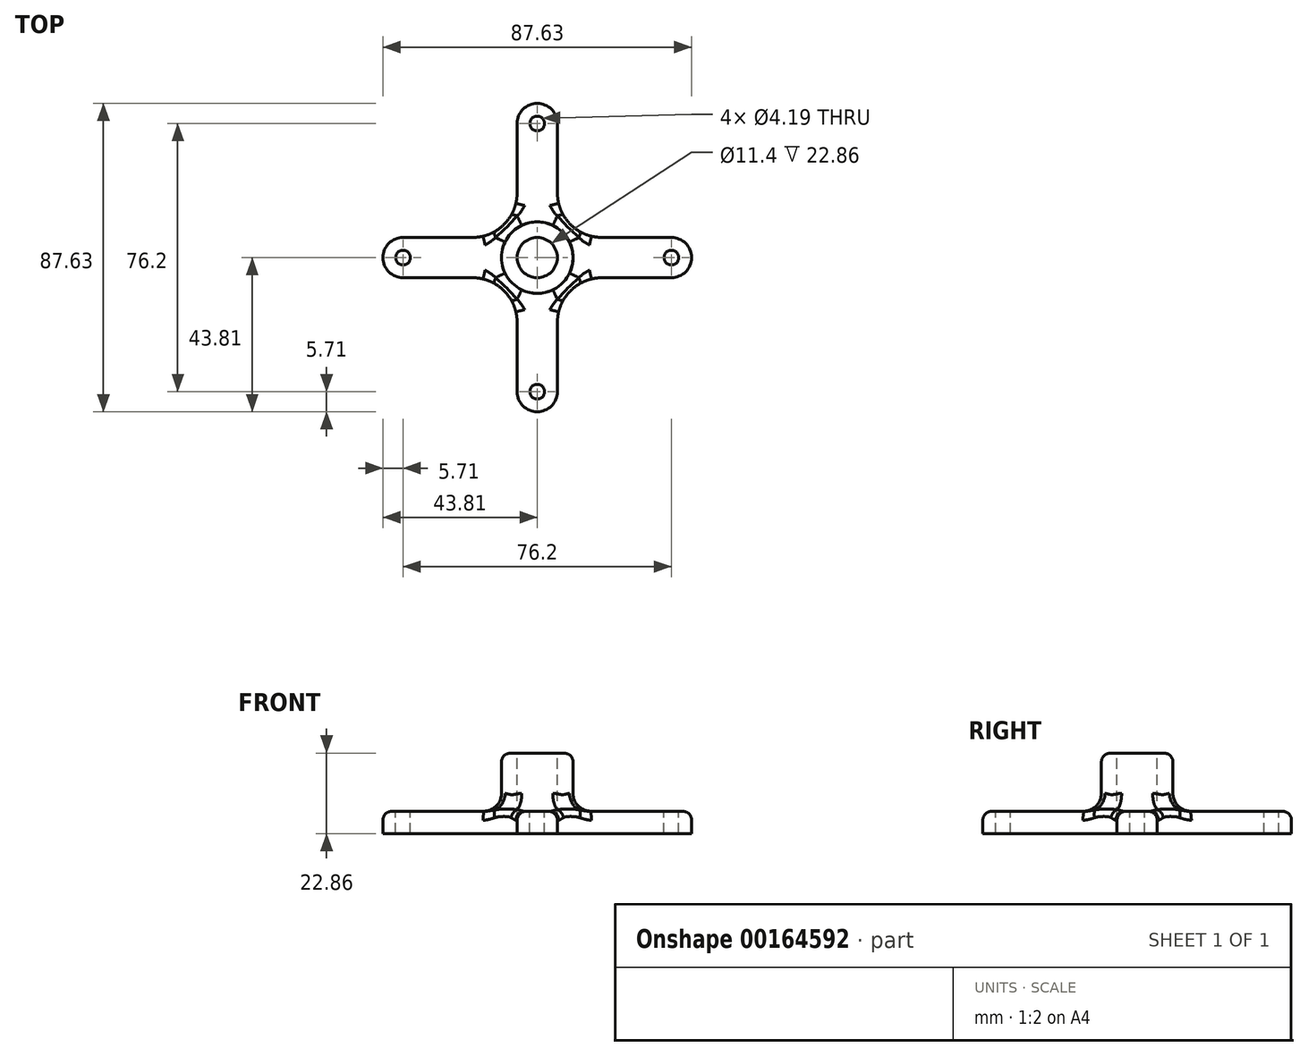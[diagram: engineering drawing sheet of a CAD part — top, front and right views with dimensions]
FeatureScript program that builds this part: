
annotation { "Feature Type Name" : "Feature", "Feature Type Description" : "" }
export const myFeature = defineFeature(function(context is Context, id is Id, definition is map)
    precondition{}
    {
        {
            var Q0;
            Q0=qCreatedBy(makeId("Top.planeOp"),FACE);
            var sketch = newSketch(context, id + "F0", { "sketchPlane" : qUnion([Q0])});
            skArc(sketch, "E0", {"start": v(5.71, 38.1) * mm, "mid": v(0, 43.81) * mm, "end": v(-5.72, 38.1) * mm});
            skArc(sketch, "E1", {"start": v(38.1, -5.71) * mm, "mid": v(43.81, 0) * mm, "end": v(38.1, 5.72) * mm});
            skArc(sketch, "E2", {"start": v(-5.72, -38.1) * mm, "mid": v(0, -43.81) * mm, "end": v(5.72, -38.1) * mm});
            skArc(sketch, "E3", {"start": v(-38.1, 5.72) * mm, "mid": v(-43.81, 0) * mm, "end": v(-38.1, -5.72) * mm});
            skLineSegment(sketch, "E4.top", {"start": v(-5.72, 1.59) * mm, "end": v(-4.64, 1.59) * mm});
            skLineSegment(sketch, "E4.left", {"start": v(-5.72, 38.1) * mm, "end": v(-5.72, 18.42) * mm});
            skLineSegment(sketch, "E4.right", {"start": v(5.71, 38.1) * mm, "end": v(5.71, 18.42) * mm});
            skPoint(sketch, "E4.middle", {"position": v(0, 19.84) * mm});
            skLineSegment(sketch, "E5.bottom", {"start": v(-38.1, -5.72) * mm, "end": v(-18.41, -5.72) * mm});
            skLineSegment(sketch, "E5.top", {"start": v(-38.1, 5.72) * mm, "end": v(-18.41, 5.72) * mm});
            skPoint(sketch, "E5.middle", {"position": v(-20.1, 0) * mm});
            skLineSegment(sketch, "E6.bottom", {"start": v(38.1, 5.72) * mm, "end": v(18.41, 5.72) * mm});
            skLineSegment(sketch, "E6.top", {"start": v(38.1, -5.72) * mm, "end": v(18.41, -5.72) * mm});
            skPoint(sketch, "E6.middle", {"position": v(16.73, 0) * mm});
            skLineSegment(sketch, "E7.top", {"start": v(-5.72, -2.38) * mm, "end": v(-4.64, -2.38) * mm});
            skLineSegment(sketch, "E7.left", {"start": v(-5.72, -38.1) * mm, "end": v(-5.72, -18.41) * mm});
            skLineSegment(sketch, "E7.right", {"start": v(5.72, -38.1) * mm, "end": v(5.72, -18.42) * mm});
            skPoint(sketch, "E7.middle", {"position": v(0, -20.24) * mm});
            skPoint(sketch, "E8.newPointA", {"position": v(-2.12, 5.72) * mm});
            skArc(sketch, "E8.filletArc", {"start": v(-18.41, 5.72) * mm, "mid": v(-9.43, 9.43) * mm, "end": v(-5.71, 18.42) * mm});
            skPoint(sketch, "E9.newPointB", {"position": v(-4.64, 5.72) * mm});
            skArc(sketch, "E9.filletArc", {"start": v(5.71, 18.42) * mm, "mid": v(9.43, 9.43) * mm, "end": v(18.41, 5.72) * mm});
            skPoint(sketch, "E10.newPointA", {"position": v(-4.64, -5.72) * mm});
            skArc(sketch, "E10.filletArc", {"start": v(18.41, -5.72) * mm, "mid": v(9.43, -9.43) * mm, "end": v(5.71, -18.42) * mm});
            skPoint(sketch, "E11.newPointB", {"position": v(-2.12, -5.72) * mm});
            skArc(sketch, "E11.filletArc", {"start": v(-5.71, -18.41) * mm, "mid": v(-9.43, -9.43) * mm, "end": v(-18.41, -5.71) * mm});
            skPoint(sketch, "E12.center.orphan", {"position": v(0, 0) * mm});
            skPoint(sketch, "E13.orphan", {"position": v(5.71, 1.59) * mm});
            skPoint(sketch, "E14.trimOffspring.end.orphan", {"position": v(5.72, -2.38) * mm});
            skCircle(sketch, "E15", {"center": v(0, 0) * mm, "radius": 10.16 * mm});
            skSolve(sketch);
        }
        {
            var Q0;
            Q0 = qSketchRegion(id + "F0", true);
            var Q1;
            Q1=makeQuery(id+"F0.imprint","IMPRINT",FACE,{"disambiguationData":[TD([[makeQuery(id+"F0.imprint","IMPRINT",EDGE,{"derivedFrom":sQuery(id+"F0.wireOp",EDGE,"E15")}),1.0]])]});
            extrude(context, id + "F1", {"entities" : qUnion([Q0, Q1]), "depth" : 6.35 * mm});
        }
        {
            var Q0;
            Q0=makeQuery(id+"F0.imprint","IMPRINT",FACE,{"disambiguationData":[TD([[makeQuery(id+"F0.imprint","IMPRINT",EDGE,{"derivedFrom":sQuery(id+"F0.wireOp",EDGE,"E15")}),1.0]])]});
            extrude(context, id + "F2", {"entities" : qUnion([Q0]), "operationType" : NewBodyOperationType.ADD, "depth" : 22.86 * mm});
        }
        {
            var Q0;
            Q0=makeQuery(id+"F2.opExtrude","CAP_FACE",FACE,{"disambiguationData":[OSD([sQuery(id+"F0.wireOp",EDGE,"E15")])],"isStart":false});
            var sketch = newSketch(context, id + "F3", { "sketchPlane" : qUnion([Q0])});
            skCircle(sketch, "E16", {"center": v(0, 0) * mm, "radius": 5.7 * mm});
            skSolve(sketch);
        }
        {
            var Q0;
            Q0 = qSketchRegion(id + "F3", true);
            extrude(context, id + "F4", {"entities" : qUnion([Q0]), "operationType" : NewBodyOperationType.REMOVE, "endBound" : BoundingType.THROUGH_ALL, "oppositeDirection" : true, "depth" : 25.4 * mm});
        }
        {
            var Q0;
            Q0=makeQuery(id+"F1.opExtrude","CAP_FACE",FACE,{"disambiguationData":[OSD([sQuery(id+"F0.wireOp",EDGE,"E0"),sQuery(id+"F0.wireOp",EDGE,"E1"),sQuery(id+"F0.wireOp",EDGE,"E2"),sQuery(id+"F0.wireOp",EDGE,"E3"),sQuery(id+"F0.wireOp",EDGE,"E4.left"),sQuery(id+"F0.wireOp",EDGE,"E4.right"),sQuery(id+"F0.wireOp",EDGE,"E5.bottom"),sQuery(id+"F0.wireOp",EDGE,"E5.top"),sQuery(id+"F0.wireOp",EDGE,"E6.bottom"),sQuery(id+"F0.wireOp",EDGE,"E6.top"),sQuery(id+"F0.wireOp",EDGE,"E7.left"),sQuery(id+"F0.wireOp",EDGE,"E7.right"),sQuery(id+"F0.wireOp",EDGE,"E8.filletArc"),sQuery(id+"F0.wireOp",EDGE,"E9.filletArc"),sQuery(id+"F0.wireOp",EDGE,"E10.filletArc"),sQuery(id+"F0.wireOp",EDGE,"E11.filletArc")])],"isStart":false});
            var sketch = newSketch(context, id + "F5", { "sketchPlane" : qUnion([Q0])});
            skCircle(sketch, "E17", {"center": v(-38.1, 0) * mm, "radius": 2.1 * mm});
            skCircle(sketch, "E18", {"center": v(0, 38.1) * mm, "radius": 2.1 * mm});
            skCircle(sketch, "E19", {"center": v(38.1, 0) * mm, "radius": 2.1 * mm});
            skCircle(sketch, "E20", {"center": v(0, -38.1) * mm, "radius": 2.1 * mm});
            skSolve(sketch);
        }
        {
            var Q0;
            Q0 = qSketchRegion(id + "F5", true);
            extrude(context, id + "F6", {"entities" : qUnion([Q0]), "operationType" : NewBodyOperationType.REMOVE, "oppositeDirection" : true, "depth" : 25.4 * mm});
        }
        {
            var Q0;
            Q0=makeQuery(id+"F2.opExtrude","CAP_EDGE",EDGE,{"disambiguationData":[OSD([sQuery(id+"F0.wireOp",EDGE,"E15")])],"isStart":false});
            fillet(context, id + "F7", {"entities" : qUnion([Q0]), "radius" : 2.54 * mm, "tangentPropagation" : true, "allowEdgeOverflow" : false});
        }
        {
            var Q0;
            Q0=makeQuery(id+"F2.boolean.opBoolean","INTERSECT",EDGE,{"derivedFrom":[makeQuery(id+"F1.opExtrude","CAP_FACE",FACE,{"disambiguationData":[OSD([sQuery(id+"F0.wireOp",EDGE,"E0"),sQuery(id+"F0.wireOp",EDGE,"E1"),sQuery(id+"F0.wireOp",EDGE,"E2"),sQuery(id+"F0.wireOp",EDGE,"E3"),sQuery(id+"F0.wireOp",EDGE,"E4.left"),sQuery(id+"F0.wireOp",EDGE,"E4.right"),sQuery(id+"F0.wireOp",EDGE,"E5.bottom"),sQuery(id+"F0.wireOp",EDGE,"E5.top"),sQuery(id+"F0.wireOp",EDGE,"E6.bottom"),sQuery(id+"F0.wireOp",EDGE,"E6.top"),sQuery(id+"F0.wireOp",EDGE,"E7.left"),sQuery(id+"F0.wireOp",EDGE,"E7.right"),sQuery(id+"F0.wireOp",EDGE,"E8.filletArc"),sQuery(id+"F0.wireOp",EDGE,"E9.filletArc"),sQuery(id+"F0.wireOp",EDGE,"E10.filletArc"),sQuery(id+"F0.wireOp",EDGE,"E11.filletArc")])],"isStart":false}),makeQuery(id+"F2.opExtrude","SWEPT_FACE",FACE,{"disambiguationData":[OSD([sQuery(id+"F0.wireOp",EDGE,"E15")])]})]});
            fillet(context, id + "F8", {"entities" : qUnion([Q0]), "radius" : 5.08 * mm, "tangentPropagation" : true, "allowEdgeOverflow" : false});
        }
        {
            var Q0;
            Q0=makeQuery(id+"F1.opExtrude","CAP_EDGE",EDGE,{"disambiguationData":[OSD([sQuery(id+"F0.wireOp",EDGE,"E5.bottom")])],"isStart":false});
            var Q1;
            Q1=makeQuery(id+"F1.opExtrude","CAP_EDGE",EDGE,{"disambiguationData":[OSD([sQuery(id+"F0.wireOp",EDGE,"E3")])],"isStart":false});
            fillet(context, id + "F9", {"entities" : qUnion([Q0, Q1]), "radius" : 2.54 * mm, "tangentPropagation" : true, "allowEdgeOverflow" : false});
        }
    });
